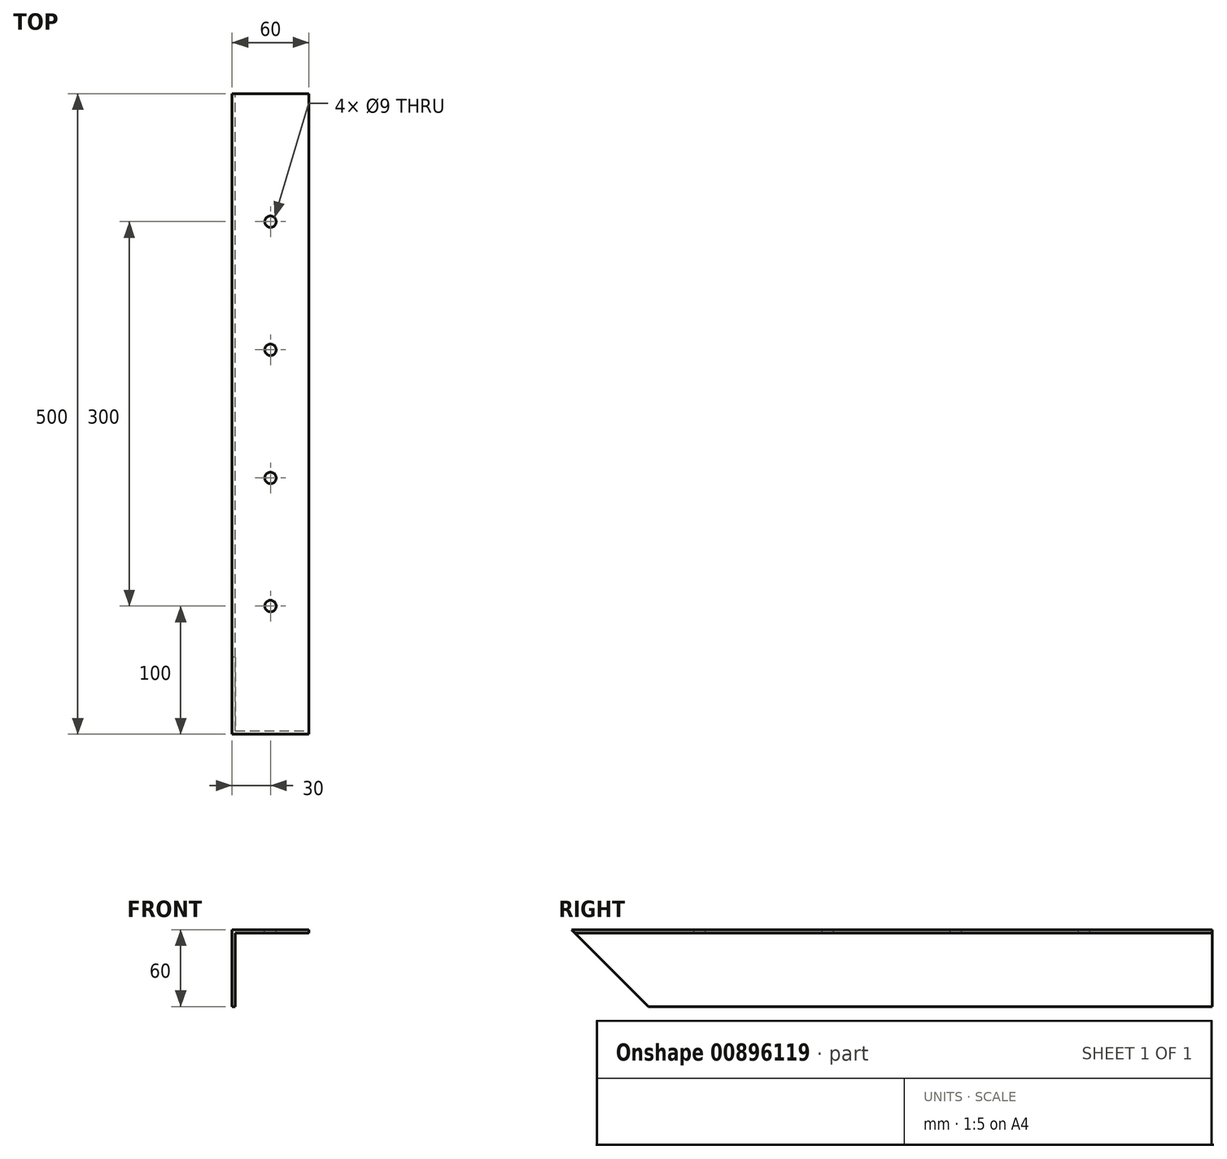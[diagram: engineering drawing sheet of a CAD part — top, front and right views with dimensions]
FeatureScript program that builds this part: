
annotation { "Feature Type Name" : "Feature", "Feature Type Description" : "" }
export const myFeature = defineFeature(function(context is Context, id is Id, definition is map)
    precondition{}
    {
        {
            var Q0;
            Q0=qCreatedBy(makeId("Front.planeOp"),FACE);
            var sketch = newSketch(context, id + "F0", { "sketchPlane" : qUnion([Q0])});
            skLineSegment(sketch, "E0", {"start": v(0, 0) * mm, "end": v(60, 0) * mm});
            skLineSegment(sketch, "E1", {"start": v(60, 0) * mm, "end": v(60, -2.5) * mm});
            skLineSegment(sketch, "E2", {"start": v(60, -2.5) * mm, "end": v(2.5, -2.5) * mm});
            skLineSegment(sketch, "E3", {"start": v(2.5, -2.5) * mm, "end": v(2.5, -60) * mm});
            skLineSegment(sketch, "E4", {"start": v(2.5, -60) * mm, "end": v(0, -60) * mm});
            skLineSegment(sketch, "E5", {"start": v(0, -60) * mm, "end": v(0, 0) * mm});
            skSolve(sketch);
        }
        {
            var Q0;
            Q0=qSketchRegion(id+"F0",true);
            extrude(context, id + "F1", {"entities" : qUnion([Q0]), "depth" : 500 * mm, "offsetDistance" : 25 * mm});
        }
        {
            var Q0;
            Q0=makeQuery(id+"F1.opExtrude","SWEPT_FACE",FACE,{"disambiguationData":[OSD([sQuery(id+"F0.wireOp",EDGE,"E5")])]});
            var sketch = newSketch(context, id + "F2", { "sketchPlane" : qUnion([Q0])});
            skLineSegment(sketch, "E6", {"start": v(500, 0) * mm, "end": v(440, -60) * mm});
            skLineSegment(sketch, "E7", {"start": v(500, 0) * mm, "end": v(500, -60) * mm});
            skLineSegment(sketch, "E8", {"start": v(500, -60) * mm, "end": v(440, -60) * mm});
            skSolve(sketch);
        }
        {
            var Q0;
            Q0=makeQuery(id+"F2.imprint","IMPRINT",FACE,{"disambiguationData":[TD([[makeQuery(id+"F2.imprint","IMPRINT",EDGE,{"derivedFrom":sQuery(id+"F2.wireOp",EDGE,"E6")}),1.0]])]});
            extrude(context, id + "F3", {"entities" : qUnion([Q0]), "operationType" : NewBodyOperationType.REMOVE, "endBound" : BoundingType.THROUGH_ALL, "oppositeDirection" : true, "depth" : 25 * mm, "offsetDistance" : 25 * mm});
        }
        {
            var Q0;
            Q0=makeQuery(id+"F1.opExtrude","SWEPT_FACE",FACE,{"disambiguationData":[OSD([sQuery(id+"F0.wireOp",EDGE,"E0")])]});
            var sketch = newSketch(context, id + "F4", { "sketchPlane" : qUnion([Q0])});
            skLineSegment(sketch, "E9", {"start": v(30, 0) * mm, "end": v(30, -100) * mm, "construction": true});
            skLineSegment(sketch, "E10", {"start": v(30, -100) * mm, "end": v(30, -200) * mm, "construction": true});
            skLineSegment(sketch, "E11", {"start": v(30, -200) * mm, "end": v(30, -300) * mm, "construction": true});
            skLineSegment(sketch, "E12", {"start": v(30, -300) * mm, "end": v(30, -400) * mm, "construction": true});
            skLineSegment(sketch, "E13", {"start": v(30, -400) * mm, "end": v(30, -500) * mm, "construction": true});
            skCircle(sketch, "E14", {"center": v(30, -100) * mm, "radius": 4.5 * mm});
            skCircle(sketch, "E15", {"center": v(30, -200) * mm, "radius": 4.5 * mm});
            skCircle(sketch, "E16", {"center": v(30, -300) * mm, "radius": 4.5 * mm});
            skCircle(sketch, "E17", {"center": v(30, -400) * mm, "radius": 4.5 * mm});
            skSolve(sketch);
        }
        {
            var Q0;
            Q0 = qSketchRegion(id + "F4", true);
            extrude(context, id + "F5", {"entities" : qUnion([Q0]), "operationType" : NewBodyOperationType.REMOVE, "endBound" : BoundingType.THROUGH_ALL, "oppositeDirection" : true, "depth" : 25 * mm, "offsetDistance" : 25 * mm});
        }
    });
